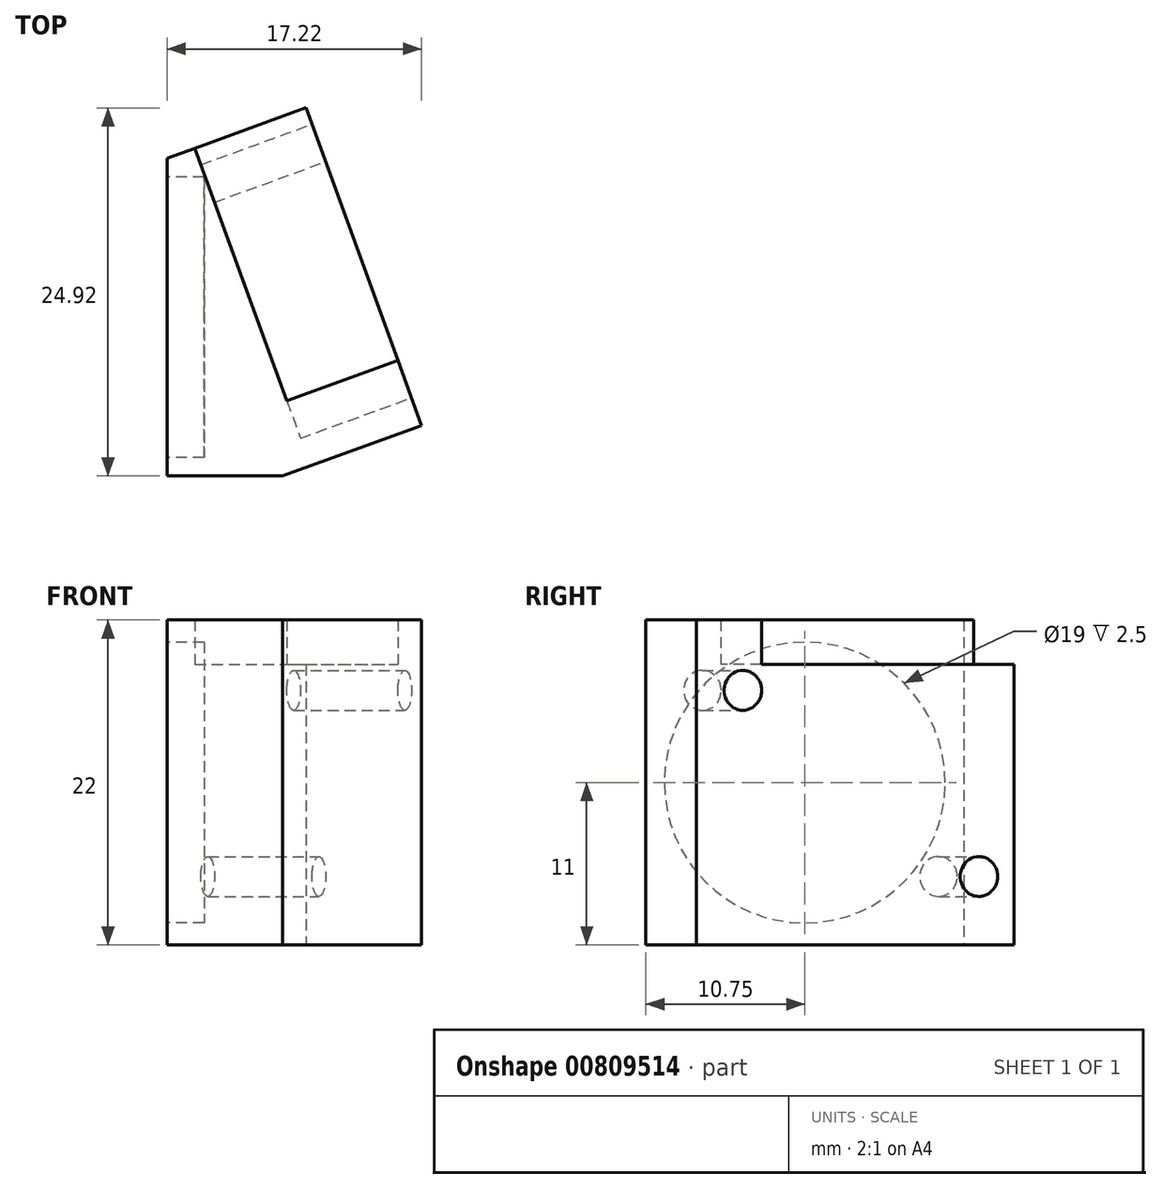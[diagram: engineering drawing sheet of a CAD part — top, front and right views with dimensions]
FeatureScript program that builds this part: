
annotation { "Feature Type Name" : "Feature", "Feature Type Description" : "" }
export const myFeature = defineFeature(function(context is Context, id is Id, definition is map)
    precondition{}
    {
        {
            var Q0;
            Q0=qCreatedBy(makeId("Top.planeOp"),FACE);
            var sketch = newSketch(context, id + "F0", { "sketchPlane" : qUnion([Q0])});
            skLineSegment(sketch, "E0", {"start": v(0, 0) * mm, "end": v(0, 21.5) * mm});
            skLineSegment(sketch, "E1", {"start": v(0, 21.5) * mm, "end": v(7.83, 0) * mm});
            skLineSegment(sketch, "E2", {"start": v(7.83, 0) * mm, "end": v(0, 0) * mm});
            skSolve(sketch);
        }
        {
            var Q0;
            Q0 = qSketchRegion(id + "F0", true);
            extrude(context, id + "F1", {"entities" : qUnion([Q0]), "depth" : 22 * mm, "offsetDistance" : 25 * mm});
        }
        {
            var Q0;
            Q0=makeQuery(id+"F1.opExtrude","SWEPT_FACE",FACE,{"disambiguationData":[OSD([sQuery(id+"F0.wireOp",EDGE,"E1")])]});
            extrude(context, id + "F2", {"entities" : qUnion([Q0]), "operationType" : NewBodyOperationType.ADD, "depth" : 10 * mm, "offsetDistance" : 25 * mm});
        }
        {
            var Q0;
            Q0=makeQuery(id+"F1.opExtrude","SWEPT_FACE",FACE,{"disambiguationData":[OSD([sQuery(id+"F0.wireOp",EDGE,"E0")])]});
            var sketch = newSketch(context, id + "F3", { "sketchPlane" : qUnion([Q0])});
            skLineSegment(sketch, "E3", {"start": v(0, 22) * mm, "end": v(-21.5, 0) * mm, "construction": true});
            skLineSegment(sketch, "E4", {"start": v(0, 0) * mm, "end": v(-10.75, 11) * mm, "construction": true});
            skCircle(sketch, "E5", {"center": v(-10.75, 11) * mm, "radius": 9.5 * mm});
            skSolve(sketch);
        }
        {
            var Q0;
            Q0 = qSketchRegion(id + "F3", true);
            extrude(context, id + "F4", {"entities" : qUnion([Q0]), "operationType" : NewBodyOperationType.REMOVE, "oppositeDirection" : true, "depth" : 2.5 * mm, "offsetDistance" : 25 * mm});
        }
        {
            var Q0;
            Q0=makeQuery(id+"F2.opExtrude","CAP_FACE",FACE,{"disambiguationData":[OSD([sQuery(id+"F0.wireOp",EDGE,"E1")])],"isStart":false});
            var sketch = newSketch(context, id + "F5", { "sketchPlane" : qUnion([Q0])});
            skCircle(sketch, "E6", {"center": v(0.66, 17.24) * mm, "radius": 1.35 * mm});
            skCircle(sketch, "E7", {"center": v(17.66, 4.64) * mm, "radius": 1.35 * mm});
            skLineSegment(sketch, "E8.bottom", {"start": v(-0.67, 22) * mm, "end": v(20.2, 22) * mm, "construction": true});
            skLineSegment(sketch, "E8.top", {"start": v(-0.67, 2.1) * mm, "end": v(20.2, 2.1) * mm, "construction": true});
            skLineSegment(sketch, "E8.right", {"start": v(20.2, 22) * mm, "end": v(20.2, 2.1) * mm, "construction": true});
            skLineSegment(sketch, "E9.bottom", {"start": v(20.2, 22) * mm, "end": v(2, 22) * mm});
            skLineSegment(sketch, "E9.top", {"start": v(20.2, 19) * mm, "end": v(2, 19) * mm});
            skLineSegment(sketch, "E9.left", {"start": v(20.2, 22) * mm, "end": v(20.2, 19) * mm});
            skLineSegment(sketch, "E9.right", {"start": v(2, 22) * mm, "end": v(2, 19) * mm});
            skSolve(sketch);
        }
        {
            var Q0;
            Q0 = qSketchRegion(id + "F5", true);
            extrude(context, id + "F6", {"entities" : qUnion([Q0]), "operationType" : NewBodyOperationType.REMOVE, "oppositeDirection" : true, "depth" : 8 * mm, "offsetDistance" : 25 * mm});
        }
    });
